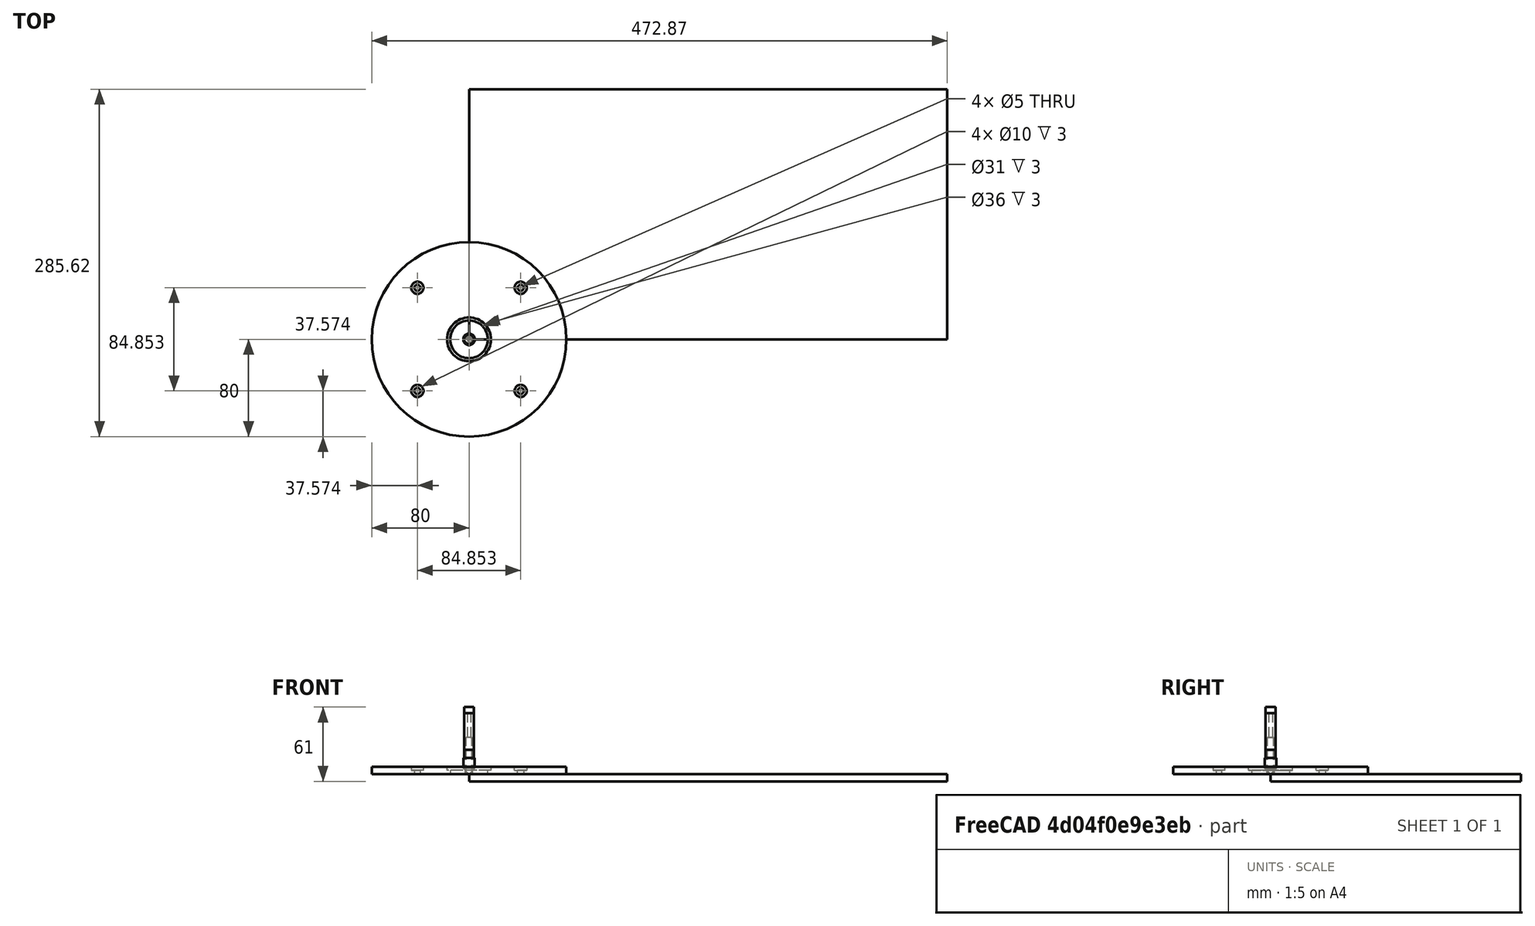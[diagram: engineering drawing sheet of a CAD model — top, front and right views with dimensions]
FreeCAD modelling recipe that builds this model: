
FCSTD DOCUMENT  (FreeCAD 0.22R36874 (Git))
Label: bushing_guide_plate
License: All rights reserved
LicenseURL: http://en.wikipedia.org/wiki/All_rights_reserved
objects: TechDraw::DrawViewDimension×19, Sketcher::SketchObject×13, PartDesign::Pocket×11, Path::FeaturePython×11, PartDesign::PolarPattern×5, Part::FeaturePython×5, App::DocumentObjectGroup×3, PartDesign::Pad×2, PartDesign::Body×2, Spreadsheet::Sheet×1, TechDraw::DrawSVGTemplate×1, App::FeaturePython×1, TechDraw::DrawViewAnnotation×1, PartDesign::Mirrored×1, TechDraw::DrawProjGroupItem×1, TechDraw::DrawProjGroup×1, TechDraw::DrawViewSection×1, TechDraw::DrawPage×1
note: 88 computed .brp shape members not serialized (recipe doc carries the construction recipe); baked Part::Feature solids carry a one-line shape summary decoded from their .brp

FEATURE [Spreadsheet::Sheet] Spreadsheet
  cells = A1='ID; B1(ID)==69 mm; D1='bushing_bore; E1(bushing_bore)==30 mm + 1 mm; A2='OD; B2(OD)==160 mm; D2='bushing_counterbore; E2(bushing_counterbore)==E1 + 5 mm; A3='mounting diameter; B3(mounting_holes_dia)==120 mm; A4='mounting hole; B4(mounting_hole)==5 mm; A7='RT0700_mounting_hole_distance_x; B7(RT0700_mounting_hole_distance_x)==106 mm; A8='RT0700_mounting_hole_distance_y; B8(RT0700_mounting_hole_distance_y)==56 mm
FEATURE [Sketcher::SketchObject] Sketch
  AttachmentSupport = -> [XY_Plane]
  FullyConstrained = true
  MapMode = 5
  expr: Constraints[0] = Spreadsheet.OD + 20 mm
  expr: Constraints[1] = Spreadsheet.ID
  expr: Constraints[5] = 6
  expr: Constraints[7] = Spreadsheet.bushing_bore
  sketch-geometry (6):
    g0: ArcOfCircle CenterX=0 CenterY=0 CenterZ=0 NormalX=0 NormalY=0 NormalZ=1 AngleXU=0 Radius=90 StartAngle=1.34693 EndAngle=4.93625
    g1: ArcOfCircle CenterX=250 CenterY=0 CenterZ=0 NormalX=0 NormalY=0 NormalZ=1 AngleXU=0 Radius=34.5 StartAngle=4.93625 EndAngle=7.63012
    g2: LineSegment StartX=19.98 StartY=87.7542 StartZ=0 EndX=257.659 EndY=33.6391 EndZ=0
    g3: LineSegment StartX=19.98 StartY=-87.7542 StartZ=0 EndX=257.659 EndY=-33.6391 EndZ=0
    g4: Circle CenterX=250 CenterY=0 CenterZ=0 NormalX=0 NormalY=0 NormalZ=1 AngleXU=0 Radius=3
    g5: Circle CenterX=0 CenterY=0 CenterZ=0 NormalX=0 NormalY=0 NormalZ=1 AngleXU=0 Radius=15.5
  constraints (13):
    c: Diameter(g0) = 180
    c: Diameter(g1) = 69
    c: Tangent(g0,g3) = -1.5708
    c: Tangent(g1,g2) = 1.5708
    c: Coincident(g4,g1)
    c: Diameter(g4) = 6
    c: Coincident(g5,g0)
    c: Diameter(g5) = 31
    c: DistanceX(g0,g1) = 250
    c: Tangent(g0,g2) = 1.5708
    c: Tangent(g1,g3) = -1.5708
    c: Coincident(g0,g-1)
    c: PointOnObject(g1,g-1)
FEATURE [PartDesign::Pad] Pad
  Direction = (0,0,1)
  Length = 6
  Length2 = 10
  Profile = -> Sketch
  ReferenceAxis = -> Sketch [N_Axis]
  Suppressed = false
  Type = 0
FEATURE [Sketcher::SketchObject] Sketch001
  AttachmentSupport = -> [Pad]
  FullyConstrained = false
  MapMode = 5
  Placement = pos=(0,0,6) rot=(0,0,1;0rad)
  expr: Constraints[1] = Spreadsheet.mounting_holes_dia
  expr: Constraints[6] = Spreadsheet.mounting_hole
  sketch-geometry (4):
    g0: Circle CenterX=0 CenterY=0 CenterZ=0 NormalX=0 NormalY=0 NormalZ=1 AngleXU=0 Radius=60
    g1: LineSegment StartX=0 StartY=0 StartZ=0 EndX=60 EndY=60 EndZ=0
    g2: GeomPoint X=42.4248 Y=42.428 Z=0
    g3: Circle CenterX=42.4248 CenterY=42.428 CenterZ=0 NormalX=0 NormalY=0 NormalZ=1 AngleXU=0 Radius=2.5
  constraints (7):
    c: Coincident(g0,g-1)
    c: Diameter(g0) = 120
    c: Coincident(g1,g0)
    c: Angle(g-1,g1) = 0.785398
    c: PointOnObject(g2,g0)
    c: Coincident(g3,g2)
    c: Diameter(g3) = 5
FEATURE [PartDesign::Pocket] Pocket
  BaseFeature = -> Pad
  Direction = (0,0,-1)
  Length = 10
  Length2 = 5
  Profile = -> Sketch001
  ReferenceAxis = -> Sketch001 [N_Axis]
  Suppressed = false
  Type = 0
FEATURE [PartDesign::PolarPattern] PolarPattern
  Angle = 360
  Axis = -> Sketch001 [N_Axis]
  BaseFeature = -> Pocket
  Mode = 0
  Occurrences = 4
  Offset = 120
  Originals = -> [Pocket]
  Suppressed = false
FEATURE [TechDraw::DrawSVGTemplate] Template
  EditableTexts = Designed_by_Name=Grzegorz Sapijaszko; Drawing_number=Drawing number; FC-Date=5/24/24; FC-SC=1 : 2; FC-SH=1 / 1; FC-Title=Bushing guide plate; Subtitle=Subtitle; Weight=Weight
  Height = 210
  Orientation = 1
  Template = <userpath>/projekty/woodworking_orig/A4_Landscape_TD.svg
  Width = 297
FEATURE [Sketcher::SketchObject] Sketch002
  AttachmentSupport = -> [PolarPattern]
  ExternalGeometry = -> [PolarPattern]
  FullyConstrained = true
  MapMode = 5
  Placement = pos=(0,0,6) rot=(0,0,1;0rad)
  expr: Constraints[1] = Spreadsheet.mounting_hole * 2
  sketch-geometry (1):
    g0: Circle CenterX=-42.428 CenterY=42.4248 CenterZ=0 NormalX=0 NormalY=0 NormalZ=1 AngleXU=0 Radius=5
  constraints (2):
    c: Coincident(g-3,g0)
    c: Diameter(g0) = 10
FEATURE [PartDesign::Pocket] Pocket001
  BaseFeature = -> PolarPattern
  Direction = (0,0,-1)
  Length = 3
  Length2 = 5
  Profile = -> Sketch002
  ReferenceAxis = -> Sketch002 [N_Axis]
  Suppressed = false
  Type = 0
FEATURE [PartDesign::PolarPattern] PolarPattern001
  Angle = 360
  Axis = -> Sketch002 [N_Axis]
  BaseFeature = -> Pocket001
  Mode = 0
  Occurrences = 4
  Offset = 120
  Originals = -> [Pocket001]
  Suppressed = false
FEATURE [Sketcher::SketchObject] Sketch003
  AttachmentSupport = -> [PolarPattern001]
  ExternalGeometry = -> [PolarPattern001]
  FullyConstrained = true
  MapMode = 5
  Placement = pos=(0,0,6) rot=(0,0,1;0rad)
  expr: Constraints[0] = 12 mm
  sketch-geometry (1):
    g0: Circle CenterX=250 CenterY=0 CenterZ=0 NormalX=0 NormalY=0 NormalZ=1 AngleXU=0 Radius=6
  constraints (2):
    c: Diameter(g0) = 12
    c: Coincident(g-3,g0)
FEATURE [PartDesign::Pocket] Pocket002
  BaseFeature = -> PolarPattern001
  Direction = (0,0,-1)
  Length = 3
  Length2 = 5
  Profile = -> Sketch003
  ReferenceAxis = -> Sketch003 [N_Axis]
  Suppressed = false
  Type = 0
FEATURE [Sketcher::SketchObject] Sketch004
  AttachmentSupport = -> [Pocket002]
  FullyConstrained = true
  MapMode = 5
  Placement = pos=(0,0,6) rot=(0,0,1;0rad)
  expr: Constraints[1] = Spreadsheet.bushing_counterbore
  sketch-geometry (1):
    g0: Circle CenterX=0 CenterY=0 CenterZ=0 NormalX=0 NormalY=0 NormalZ=1 AngleXU=0 Radius=18
  constraints (2):
    c: Coincident(g0,g-1)
    c: Diameter(g0) = 36
FEATURE [PartDesign::Pocket] Pocket003
  BaseFeature = -> Pocket002
  Direction = (0,0,-1)
  Length = 3
  Length2 = 5
  Profile = -> Sketch004
  ReferenceAxis = -> Sketch004 [N_Axis]
  Suppressed = false
  Type = 0
FEATURE [Sketcher::SketchObject] Sketch006
  AttachmentSupport = -> [XY_Plane002]
  FullyConstrained = true
  MapMode = 5
  expr: Constraints[1] = Spreadsheet.OD
  expr: Constraints[3] = Spreadsheet.bushing_bore
  sketch-geometry (2):
    g0: Circle CenterX=0 CenterY=0 CenterZ=0 NormalX=0 NormalY=0 NormalZ=1 AngleXU=0 Radius=80
    g1: Circle CenterX=0 CenterY=0 CenterZ=0 NormalX=0 NormalY=0 NormalZ=1 AngleXU=0 Radius=15.5
  constraints (4):
    c: Coincident(g0,g-1)
    c: Diameter(g0) = 160
    c: Coincident(g1,g0)
    c: Diameter(g1) = 31
FEATURE [PartDesign::Pad] Pad002
  Direction = (0,0,1)
  Length = 6
  Length2 = 10
  Profile = -> Sketch006
  ReferenceAxis = -> Sketch006 [N_Axis]
  Suppressed = false
  Type = 0
FEATURE [Sketcher::SketchObject] Sketch007
  AttachmentSupport = -> [Pad002]
  FullyConstrained = true
  MapMode = 5
  Placement = pos=(0,0,6) rot=(0,0,1;0rad)
  expr: Constraints[1] = Spreadsheet.mounting_holes_dia
  expr: Constraints[6] = Spreadsheet.mounting_hole
  sketch-geometry (3):
    g0: Circle CenterX=0 CenterY=0 CenterZ=0 NormalX=0 NormalY=0 NormalZ=1 AngleXU=0 Radius=60
    g1: LineSegment StartX=0 StartY=0 StartZ=0 EndX=42.4264 EndY=42.4264 EndZ=0
    g2: Circle CenterX=42.4264 CenterY=42.4264 CenterZ=0 NormalX=0 NormalY=0 NormalZ=1 AngleXU=0 Radius=2.5
  constraints (7):
    c: Coincident(g0,g-1)
    c: Diameter(g0) = 120
    c: Coincident(g1,g0)
    c: PointOnObject(g1,g0)
    c: Angle(g-1,g1) = 0.785398
    c: Coincident(g2,g1)
    c: Diameter(g2) = 5
FEATURE [PartDesign::Pocket] Pocket004
  BaseFeature = -> Pad002
  Direction = (0,0,-1)
  Length = 6
  Length2 = 5
  Profile = -> Sketch007
  ReferenceAxis = -> Sketch007 [N_Axis]
  Suppressed = false
  Type = 0
FEATURE [PartDesign::PolarPattern] PolarPattern002
  Angle = 360
  Axis = -> Sketch007 [N_Axis]
  BaseFeature = -> Pocket004
  Mode = 0
  Occurrences = 4
  Offset = 120
  Originals = -> [Pocket004]
  Suppressed = false
FEATURE [Sketcher::SketchObject] Sketch008
  AttachmentSupport = -> [PolarPattern002]
  ExternalGeometry = -> [PolarPattern002]
  FullyConstrained = true
  MapMode = 5
  Placement = pos=(0,0,6) rot=(0,0,1;0rad)
  expr: Constraints[1] = Spreadsheet.mounting_hole * 2
  sketch-geometry (1):
    g0: Circle CenterX=42.4264 CenterY=42.4264 CenterZ=0 NormalX=0 NormalY=0 NormalZ=1 AngleXU=0 Radius=5
  constraints (2):
    c: Coincident(g0,g-3)
    c: Diameter(g0) = 10
FEATURE [PartDesign::Pocket] Pocket005
  BaseFeature = -> PolarPattern002
  Direction = (0,0,-1)
  Length = 3
  Length2 = 5
  Profile = -> Sketch008
  ReferenceAxis = -> Sketch008 [N_Axis]
  Suppressed = false
  Type = 0
FEATURE [PartDesign::PolarPattern] PolarPattern003
  Angle = 360
  Axis = -> Sketch008 [N_Axis]
  BaseFeature = -> Pocket005
  Mode = 0
  Occurrences = 4
  Offset = 120
  Originals = -> [Pocket005]
  Suppressed = false
FEATURE [Sketcher::SketchObject] Sketch009
  AttachmentSupport = -> [PolarPattern003]
  FullyConstrained = true
  MapMode = 5
  Placement = pos=(0,0,6) rot=(0,0,1;0rad)
  expr: Constraints[1] = Spreadsheet.bushing_counterbore
  sketch-geometry (1):
    g0: Circle CenterX=0 CenterY=0 CenterZ=0 NormalX=0 NormalY=0 NormalZ=1 AngleXU=0 Radius=18
  constraints (2):
    c: Coincident(g0,g-1)
    c: Diameter(g0) = 36
FEATURE [PartDesign::Pocket] Pocket006
  BaseFeature = -> PolarPattern003
  Direction = (0,0,-1)
  Length = 3
  Length2 = 5
  Profile = -> Sketch009
  ReferenceAxis = -> Sketch009 [N_Axis]
  Suppressed = false
  Type = 0
FEATURE [PartDesign::Body] Body002  label="bushing_base_plate"
  Group = -> [Sketch006,Pad002,Sketch007,Pocket004,PolarPattern002,Sketch008,Pocket005,PolarPattern003,Sketch009,Pocket006]
  Origin = -> Origin002
  Tip = -> Pocket006
FEATURE [App::FeaturePython] SetupSheet  # Path/CAM operation (typed FeaturePython)
  ClearanceHeightExpression = OpStockZMax+SetupSheet.ClearanceHeightOffset
  ClearanceHeightOffset = 5
  CoolantMode = 0
  CoolantModes = None | Flood | Mist
  FinalDepthExpression = OpFinalDepth
  HorizRapid = 20
  SafeHeightExpression = OpStockZMax+SetupSheet.SafeHeightOffset
  SafeHeightOffset = 3
  StartDepthExpression = OpStartDepth
  StepDownExpression = OpToolDiameter
  VertRapid = 2
FEATURE [Part::FeaturePython] ToolBit  label="Endmill D=6, H=20, S=8"  # Path/CAM toolbit (typed FeaturePython)
  BitPropertyNames = Chipload | CuttingEdgeHeight | Diameter | Flutes | Length | Material | ShankDiameter | SpindleDirection
  BitShape = <path>
  Chipload = 0
  CuttingEdgeHeight = 20
  Diameter = 6
  Flutes = 2
  Length = 50
  Material = 0
  ShankDiameter = 8
  ShapeName = endmill
  SpindleDirection = 0
FEATURE [Path::FeaturePython] TC__Endmill_D_6__H_20__S_8  label="TC: Endmill D=6, H=20, S=8"  # Path/CAM operation (typed FeaturePython)
  HorizFeed = 20
  HorizRapid = 20
  SpindleDir = 0
  SpindleSpeed = 0
  Tool = -> ToolBit
  ToolNumber = 16
  VertFeed = 1.5
  VertRapid = 2
  expr: HorizRapid = SetupSheet.HorizRapid
  expr: VertRapid = SetupSheet.VertRapid
FEATURE [Part::FeaturePython] ToolBit001  label="5mm Endmill"  # Path/CAM toolbit (typed FeaturePython)
  BitPropertyNames = Chipload | CuttingEdgeHeight | Diameter | Flutes | Length | Material | ShankDiameter | SpindleDirection
  BitShape = <userpath>/.local/share/FreeCAD/Macro/Tools/Shape/endmill.fcstd
  Chipload = 0
  CuttingEdgeHeight = 30
  Diameter = 5
  File = <userpath>/.local/share/FreeCAD/Macro/Tools/Bit/5mm_Endmill.fctb
  Flutes = 0
  Length = 50
  Material = 0
  ShankDiameter = 3
  ShapeName = endmill
  SpindleDirection = 0
FEATURE [Path::FeaturePython] TC__5mm_Endmill  label="TC: 5mm Endmill"  # Path/CAM operation (typed FeaturePython)
  HorizFeed = 15
  HorizRapid = 20
  SpindleDir = 0
  SpindleSpeed = 0
  Tool = -> ToolBit001
  ToolNumber = 1
  VertFeed = 2
  VertRapid = 2
  expr: HorizRapid = SetupSheet.HorizRapid
  expr: VertRapid = SetupSheet.VertRapid
FEATURE [Part::FeaturePython] ToolBit002  label="V-bit D=9.5, H=12.7, S=8"  # Path/CAM toolbit (typed FeaturePython)
  BitPropertyNames = Chipload | CuttingEdgeAngle | CuttingEdgeHeight | Diameter | Flutes | Length | Material | ShankDiameter | TipDiameter
  BitShape = <userpath>/.local/share/FreeCAD/Macro/Tools/Shape/vbit.fcstd
  Chipload = 0
  CuttingEdgeAngle = 90
  CuttingEdgeHeight = 8.5
  Diameter = 9.5
  File = <userpath>/.local/share/FreeCAD/Macro/Tools/Bit/1389a496-7324-11ee-af98-1065300da2fe.fctb
  Flutes = 2
  Length = 55
  Material = 0
  ShankDiameter = 8
  ShapeName = vbit
  TipDiameter = 0.1
FEATURE [Path::FeaturePython] TC__V_bit_D_9_5__H_12_7__S_8  label="TC: V-bit D=9.5, H=12.7, S=8"  # Path/CAM operation (typed FeaturePython)
  HorizFeed = 15
  HorizRapid = 20
  SpindleDir = 0
  SpindleSpeed = 0
  Tool = -> ToolBit002
  ToolNumber = 15
  VertFeed = 1
  VertRapid = 2
  expr: HorizRapid = SetupSheet.HorizRapid
  expr: VertRapid = SetupSheet.VertRapid
FEATURE [App::DocumentObjectGroup] Tools
  Group = -> [TC__Endmill_D_6__H_20__S_8,TC__5mm_Endmill,TC__V_bit_D_9_5__H_12_7__S_8]
FEATURE [Sketcher::SketchObject] Sketch010
  AttachmentSupport = -> [Pocket003]
  FullyConstrained = true
  MapMode = 5
  Placement = pos=(0,0,6) rot=(0,0,1;0rad)
  expr: Constraints[0] = Spreadsheet.RT0700_mounting_hole_distance_x / 2
  expr: Constraints[1] = Spreadsheet.RT0700_mounting_hole_distance_y / 2
  expr: Constraints[2] = Spreadsheet.mounting_hole
  expr: Constraints[3] = Spreadsheet.RT0700_mounting_hole_distance_x / 2
  expr: Constraints[4] = Spreadsheet.RT0700_mounting_hole_distance_y / 2
  expr: Constraints[5] = Spreadsheet.mounting_hole
  sketch-geometry (2):
    g0: Circle CenterX=53 CenterY=28 CenterZ=0 NormalX=0 NormalY=0 NormalZ=1 AngleXU=0 Radius=2.5
    g1: Circle CenterX=53 CenterY=-28 CenterZ=0 NormalX=0 NormalY=0 NormalZ=1 AngleXU=0 Radius=2.5
  constraints (6):
    c: DistanceX(g-1,g0) = 53
    c: DistanceY(g-1,g0) = 28
    c: Diameter(g0) = 5
    c: DistanceX(g-1,g1) = 53
    c: DistanceY(g1,g-1) = 28
    c: Diameter(g1) = 5
FEATURE [PartDesign::Pocket] Pocket007
  BaseFeature = -> Pocket003
  Direction = (0,0,-1)
  Length = 6
  Length2 = 5
  Profile = -> Sketch010
  ReferenceAxis = -> Sketch010 [N_Axis]
  Suppressed = false
  Type = 0
FEATURE [Sketcher::SketchObject] Sketch011
  AttachmentSupport = -> [Pocket007]
  ExternalGeometry = -> [Pocket007]
  FullyConstrained = true
  MapMode = 5
  Placement = pos=(0,0,6) rot=(0,0,1;0rad)
  expr: Constraints[1] = Spreadsheet.RT0700_mounting_hole_distance_x / 2
  expr: Constraints[2] = Spreadsheet.RT0700_mounting_hole_distance_y / 2
  expr: Constraints[4] = Spreadsheet.RT0700_mounting_hole_distance_x / 2
  expr: Constraints[5] = Spreadsheet.RT0700_mounting_hole_distance_y / 2
  sketch-geometry (2):
    g0: Circle CenterX=53 CenterY=28 CenterZ=0 NormalX=0 NormalY=0 NormalZ=1 AngleXU=0 Radius=5
    g1: Circle CenterX=53 CenterY=-28 CenterZ=0 NormalX=0 NormalY=0 NormalZ=1 AngleXU=0 Radius=5
  constraints (6):
    c: Diameter(g0) = 10
    c: DistanceX(g-1,g0) = 53
    c: DistanceY(g-1,g0) = 28
    c: Diameter(g1) = 10
    c: DistanceX(g-1,g1) = 53
    c: DistanceY(g1,g-1) = 28
FEATURE [PartDesign::Pocket] Pocket008
  BaseFeature = -> Pocket007
  Direction = (0,0,-1)
  Length = 3
  Length2 = 5
  Profile = -> Sketch011
  ReferenceAxis = -> Sketch011 [N_Axis]
  Suppressed = false
  Type = 0
FEATURE [PartDesign::PolarPattern] PolarPattern004
  Angle = 360
  Axis = -> Sketch010 [N_Axis]
  BaseFeature = -> Pocket008
  Mode = 0
  Occurrences = 4
  Offset = 120
  Originals = -> [Pocket007,Pocket008]
  Suppressed = false
FEATURE [TechDraw::DrawViewAnnotation] Annotation
  Font = osifont
  LineSpace = 100
  LockPosition = false
  MaxWidth = -1
  Rotation = 0
  ScaleType = 0
  Text = 2024-05-23: added mounting holes |        for plunge and trimer bases  |        for Makita RT0700
  TextSize = 4
  TextStyle = 0
  X = 65.4035
  Y = 31.8309
FEATURE [Sketcher::SketchObject] Sketch012
  AttachmentSupport = -> [PolarPattern004]
  FullyConstrained = true
  MapMode = 5
  Placement = pos=(0,0,6) rot=(0,0,1;0rad)
  expr: Constraints[4] = Spreadsheet.mounting_hole
  expr: Constraints[5] = 27.5 mm
  expr: Constraints[7] = Spreadsheet.mounting_hole
  sketch-geometry (3):
    g0: Circle CenterX=0 CenterY=0 CenterZ=0 NormalX=0 NormalY=0 NormalZ=1 AngleXU=0 Radius=35.5
    g1: Circle CenterX=28 CenterY=-25 CenterZ=0 NormalX=0 NormalY=0 NormalZ=1 AngleXU=0 Radius=2.5
    g2: Circle CenterX=27.5 CenterY=20 CenterZ=0 NormalX=0 NormalY=0 NormalZ=1 AngleXU=0 Radius=2.5
  constraints (8):
    c: Coincident(g0,g-1)
    c: Diameter(g0) = 71
    c: DistanceY(g1,g0) = 25
    c: DistanceX(g0,g1) = 28
    c: Diameter(g1) = 5
    c: DistanceX(g0,g2) = 27.5
    c: DistanceY(g0,g2) = 20
    c: Diameter(g2) = 5
FEATURE [PartDesign::Pocket] Pocket009
  BaseFeature = -> PolarPattern004
  Direction = (0,0,-1)
  Length = 6
  Length2 = 5
  Profile = -> Sketch012
  ReferenceAxis = -> Sketch012 [N_Axis]
  Suppressed = false
  Type = 0
FEATURE [Sketcher::SketchObject] Sketch013
  AttachmentSupport = -> [Pocket009]
  ExternalGeometry = -> [Pocket009]
  FullyConstrained = true
  MapMode = 5
  Placement = pos=(0,0,6) rot=(0,0,1;0rad)
  sketch-geometry (2):
    g0: Circle CenterX=27.5 CenterY=20 CenterZ=0 NormalX=0 NormalY=0 NormalZ=1 AngleXU=0 Radius=5
    g1: Circle CenterX=28 CenterY=-25 CenterZ=0 NormalX=0 NormalY=0 NormalZ=1 AngleXU=0 Radius=5
  constraints (4):
    c: Coincident(g0,g-3)
    c: Coincident(g1,g-4)
    c: Diameter(g1) = 10
    c: Diameter(g0) = 10
FEATURE [PartDesign::Pocket] Pocket010
  BaseFeature = -> Pocket009
  Direction = (0,0,-1)
  Length = 3
  Length2 = 5
  Profile = -> Sketch013
  ReferenceAxis = -> Sketch013 [N_Axis]
  Suppressed = false
  Type = 0
FEATURE [PartDesign::Mirrored] Mirrored
  BaseFeature = -> Pocket010
  MirrorPlane = -> Sketch013 [V_Axis]
  Originals = -> [Pocket010,Pocket009]
  Suppressed = false
FEATURE [PartDesign::Body] Body  label="bushing_guide_plate"
  Group = -> [Sketch,Pad,Sketch001,Pocket,PolarPattern,Sketch002,Pocket001,PolarPattern001,Sketch003,Pocket002,Sketch004,Pocket003,Sketch010,Pocket007,Sketch011,Pocket008,PolarPattern004,Sketch012,Pocket009,Sketch013,Pocket010,Mirrored]
  Origin = -> Origin
  Tip = -> Mirrored
FEATURE [TechDraw::DrawProjGroupItem] ProjItem  label="Front"
  CoarseView = false
  Direction = (0,0,1)
  Focus = 100
  HardHidden = false
  IsoCount = 0
  IsoHidden = false
  IsoVisible = false
  LockPosition = true
  Perspective = false
  Rotation = 0
  RotationVector = (1,0,0)
  Scale = 0.5
  ScaleType = 2
  ScrubCount = 0
  SeamHidden = false
  SeamVisible = false
  SmoothHidden = false
  SmoothVisible = true
  Source = -> [Body]
  Type = 0
  X = 0
  XDirection = (1,0,0)
  Y = 0
FEATURE [TechDraw::DrawProjGroup] ProjGroup
  Anchor = -> ProjItem
  AutoDistribute = true
  LockPosition = false
  ProjectionType = 0
  Rotation = 0
  Scale = 0.5
  ScaleType = 2
  Source = -> [Body]
  Views = -> [ProjItem]
  X = 150
  Y = 145
  spacingX = 15
  spacingY = 15
FEATURE [TechDraw::DrawViewSection] SectionView  label="Section  - "
  BaseView = -> ProjItem
  CoarseView = false
  CutSurfaceDisplay = 2
  Direction = (1e-16,-1,0)
  FileGeomPattern = <path>
  FileHatchPattern = <path>
  Focus = 100
  FuseBeforeCut = false
  HardHidden = false
  HatchOffset = (0,0,0)
  HatchRotation = 0
  HatchScale = 1
  IsoCount = 0
  IsoHidden = false
  IsoVisible = false
  LockPosition = false
  NameGeomPattern = Diamond
  Perspective = false
  Rotation = 0
  Scale = 0.5
  ScaleType = 2
  ScrubCount = 0
  SeamHidden = false
  SeamVisible = false
  SectionDirection = 4
  SectionLineStretch = 1
  SectionNormal = (1e-16,-1,0)
  SectionOrigin = (97.29,-0.05,5)
  SmoothHidden = false
  SmoothVisible = true
  Source = -> [Body]
  TrimAfterCut = false
  UsePreviousCut = false
  X = 150
  XDirection = (1,1e-16,0)
  Y = 70
FEATURE [TechDraw::DrawViewDimension] Dimension
  AngleOverride = false
  Arbitrary = false
  ArbitraryTolerances = false
  BoxCorners = (2) [(-93.625,-1.5,-1e-07),(93.625,1.5,1e-07)]
  EqualTolerance = true
  ExtensionAngle = 0
  FormatSpec = ⌀%.2w
  FormatSpecOverTolerance = %+.2w
  FormatSpecUnderTolerance = %+.2w
  Inverted = false
  LineAngle = 0
  LockPosition = false
  MeasureType = 1
  OverTolerance = 0
  References2D = -> [SectionView]
  Rotation = 0
  ScaleType = 0
  TheoreticalExact = false
  Type = 1
  UnderTolerance = 0
  X = -48.625
  Y = -2.70318
FEATURE [TechDraw::DrawViewDimension] Dimension002
  AngleOverride = false
  Arbitrary = false
  ArbitraryTolerances = false
  BoxCorners = (2) [(-93.625,-1.5,-1e-07),(93.625,1.5,1e-07)]
  EqualTolerance = true
  ExtensionAngle = 0
  FormatSpec = ⌀%.2w
  FormatSpecOverTolerance = %+.2w
  FormatSpecUnderTolerance = %+.2w
  Inverted = false
  LineAngle = 0
  LockPosition = false
  MeasureType = 1
  OverTolerance = 0
  References2D = -> [SectionView]
  Rotation = 0
  ScaleType = 0
  TheoreticalExact = false
  Type = 1
  UnderTolerance = 0
  X = -48.625
  Y = 12.5693
FEATURE [TechDraw::DrawViewDimension] Dimension006
  AngleOverride = false
  Arbitrary = false
  ArbitraryTolerances = false
  BoxCorners = (2) [(-93.625,-45,0),(93.625,45,0)]
  EqualTolerance = true
  ExtensionAngle = 0
  FormatSpec = R%.2w
  FormatSpecOverTolerance = %+.2w
  FormatSpecUnderTolerance = %+.2w
  Inverted = false
  LineAngle = 0
  LockPosition = false
  MeasureType = 1
  OverTolerance = 0
  References2D = -> [ProjItem]
  Rotation = 0
  ScaleType = 0
  TheoreticalExact = false
  Type = 4
  UnderTolerance = 0
  X = 99.6814
  Y = 13.0174
FEATURE [TechDraw::DrawViewDimension] Dimension008
  AngleOverride = false
  Arbitrary = false
  ArbitraryTolerances = false
  BoxCorners = (2) [(-93.625,-45,0),(93.625,45,0)]
  EqualTolerance = true
  ExtensionAngle = 0
  FormatSpec = R%.2w
  FormatSpecOverTolerance = %+.2w
  FormatSpecUnderTolerance = %+.2w
  Inverted = false
  LineAngle = 0
  LockPosition = false
  MeasureType = 1
  OverTolerance = 0
  References2D = -> [ProjItem]
  Rotation = 0
  ScaleType = 0
  TheoreticalExact = false
  Type = 4
  UnderTolerance = 0
  X = -54.8187
  Y = 39.2993
FEATURE [TechDraw::DrawViewDimension] Dimension010
  AngleOverride = false
  Arbitrary = false
  ArbitraryTolerances = false
  BoxCorners = (2) [(-93.625,-1.5,-1e-07),(93.625,1.5,1e-07)]
  EqualTolerance = true
  ExtensionAngle = 0
  FormatSpec = %.2w
  FormatSpecOverTolerance = %+.2w
  FormatSpecUnderTolerance = %+.2w
  Inverted = false
  LineAngle = 0
  LockPosition = false
  MeasureType = 1
  OverTolerance = 0
  References2D = -> [SectionView]
  Rotation = 0
  ScaleType = 0
  TheoreticalExact = false
  Type = 2
  UnderTolerance = 0
  X = -100.968
  Y = 2.5
FEATURE [Part::FeaturePython] Clone  label="Model-bushing_guide_plate"  # Draft clone (typed FeaturePython)
  AttacherType = Attacher::AttachEngine3D
  Fuse = false
  Objects = -> [Body]
  PathResource = Model
  Placement = pos=(105,104.973,-6) rot=(0,0,-1;0.226893rad)
  Scale = (1,1,1)
FEATURE [App::DocumentObjectGroup] Model
  Group = -> [Clone]
FEATURE [Part::FeaturePython] Stock  # WARN: FeaturePython — macro-defined, semantics opaque (R4)
  Base = -> Model
  ExtXneg = 15
  ExtXpos = 10
  ExtYneg = 15
  ExtYpos = 10
  ExtZneg = 0
  ExtZpos = 0
  Placement = pos=(15,15,-6) rot=(0,0,1;0rad)
  StockType = FromBase
FEATURE [Path::FeaturePython] Adaptive  # Path/CAM operation (typed FeaturePython)
  Active = true
  Base = -> [Clone]
  ClearanceHeight = 5
  CoolantMode = 0
  CycleTime = 00:18:50
  ExtensionCorners = true
  ExtensionLengthDefault = 3
  FinalDepth = -3
  FinishDepth = 0
  FinishingProfile = true
  ForceInsideOut = false
  HelixAngle = 5
  HelixConeAngle = 0
  HelixDiameterLimit = 1
  KeepToolDownRatio = 3
  LiftDistance = 0
  OpFinalDepth = 0
  OpStartDepth = 1
  OpStockZMax = 0
  OpStockZMin = -6
  OpToolDiameter = 6
  OperationType = 1
  SafeHeight = 3
  Side = 1
  StartDepth = 0
  StepDown = 1
  StepOver = 20
  StockToLeave = 0
  StopProcessing = false
  Stopped = false
  Tolerance = 0.1
  ToolController = -> TC__Endmill_D_6__H_20__S_8
  UseHelixArcs = false
  UseOutline = false
  expr: ClearanceHeight = OpStockZMax + SetupSheet.ClearanceHeightOffset
  expr: ExtensionLengthDefault = OpToolDiameter / 2
  expr: FinalDepth = -3 mm
  expr: SafeHeight = OpStockZMax + SetupSheet.SafeHeightOffset
  expr: StartDepth = 0
  expr: StepDown = 1 mm
FEATURE [Path::FeaturePython] Adaptive001  # Path/CAM operation (typed FeaturePython)
  Active = true
  Base = -> [Clone]
  ClearanceHeight = 5
  CoolantMode = 0
  CycleTime = 00:02:35
  ExtensionCorners = true
  ExtensionLengthDefault = 3
  FinalDepth = -3
  FinishDepth = 0
  FinishingProfile = true
  ForceInsideOut = false
  HelixAngle = 5
  HelixConeAngle = 0
  HelixDiameterLimit = 0
  KeepToolDownRatio = 3
  LiftDistance = 0
  OpFinalDepth = -3
  OpStartDepth = 0
  OpStockZMax = 0
  OpStockZMin = -6
  OpToolDiameter = 6
  OperationType = 0
  SafeHeight = 3
  Side = 1
  StartDepth = 0
  StepDown = 1
  StepOver = 30
  StockToLeave = 0
  StopProcessing = false
  Stopped = false
  Tolerance = 0.1
  ToolController = -> TC__Endmill_D_6__H_20__S_8
  UseHelixArcs = false
  UseOutline = false
  expr: ClearanceHeight = OpStockZMax + SetupSheet.ClearanceHeightOffset
  expr: ExtensionLengthDefault = OpToolDiameter / 2
  expr: FinalDepth = OpFinalDepth
  expr: SafeHeight = OpStockZMax + SetupSheet.SafeHeightOffset
  expr: StartDepth = OpStartDepth
  expr: StepDown = 1
FEATURE [Path::FeaturePython] Adaptive002  # Path/CAM operation (typed FeaturePython)
  Active = true
  Base = -> [Clone]
  ClearanceHeight = 5
  CoolantMode = 0
  CycleTime = 00:03:15
  ExtensionCorners = true
  ExtensionLengthDefault = 3
  FinalDepth = -7
  FinishDepth = 0
  FinishingProfile = true
  ForceInsideOut = false
  HelixAngle = 5
  HelixConeAngle = 0
  HelixDiameterLimit = 0
  KeepToolDownRatio = 3
  LiftDistance = 0
  OpFinalDepth = -6
  OpStartDepth = 0
  OpStockZMax = 0
  OpStockZMin = -6
  OpToolDiameter = 6
  OperationType = 0
  SafeHeight = 3
  Side = 1
  StartDepth = -3
  StepDown = 1
  StepOver = 30
  StockToLeave = 0
  StopProcessing = false
  Stopped = false
  Tolerance = 0.1
  ToolController = -> TC__Endmill_D_6__H_20__S_8
  UseHelixArcs = false
  UseOutline = false
  expr: ClearanceHeight = OpStockZMax + SetupSheet.ClearanceHeightOffset
  expr: ExtensionLengthDefault = OpToolDiameter / 2
  expr: FinalDepth = OpFinalDepth - 1 mm
  expr: SafeHeight = OpStockZMax + SetupSheet.SafeHeightOffset
  expr: StartDepth = -3 mm
  expr: StepDown = 1
FEATURE [Path::FeaturePython] Adaptive003  # Path/CAM operation (typed FeaturePython)
  Active = true
  Base = -> [Clone]
  ClearanceHeight = 5
  CoolantMode = 0
  CycleTime = 01:13:24
  ExtensionCorners = true
  ExtensionLengthDefault = 2.5
  FinalDepth = -7
  FinishDepth = 0
  FinishingProfile = true
  ForceInsideOut = false
  HelixAngle = 5
  HelixConeAngle = 0
  HelixDiameterLimit = 0
  KeepToolDownRatio = 3
  LiftDistance = 0
  OpFinalDepth = -6
  OpStartDepth = 0
  OpStockZMax = 0
  OpStockZMin = -6
  OpToolDiameter = 5
  OperationType = 1
  SafeHeight = 3
  Side = 0
  StartDepth = 0
  StepDown = 1
  StepOver = 40
  StockToLeave = 0.5
  StopProcessing = false
  Stopped = false
  Tolerance = 0.05
  ToolController = -> TC__5mm_Endmill
  UseHelixArcs = false
  UseOutline = false
  expr: ClearanceHeight = OpStockZMax + SetupSheet.ClearanceHeightOffset
  expr: ExtensionLengthDefault = OpToolDiameter / 2
  expr: FinalDepth = OpFinalDepth - 1 mm
  expr: SafeHeight = OpStockZMax + SetupSheet.SafeHeightOffset
  expr: StartDepth = OpStartDepth
  expr: StepDown = 1
FEATURE [Path::FeaturePython] Drilling  # Path/CAM operation (typed FeaturePython)
  Active = true
  AddTipLength = false
  Base = -> [Clone]
  ClearanceHeight = 5
  CoolantMode = 0
  CycleTime = 00:00:33
  DwellEnabled = false
  DwellTime = 1
  ExtraOffset = 0
  FinalDepth = -7
  KeepToolDown = false
  OpFinalDepth = -6
  OpStartDepth = 0
  OpStockZMax = 0
  OpStockZMin = -6
  OpToolDiameter = 5
  PeckDepth = 1
  PeckEnabled = true
  RetractHeight = 0
  RetractMode = 0
  SafeHeight = 3
  StartDepth = -3
  ToolController = -> TC__5mm_Endmill
  chipBreakEnabled = false
  feedRetractEnabled = false
  expr: ClearanceHeight = OpStockZMax + SetupSheet.ClearanceHeightOffset
  expr: FinalDepth = OpFinalDepth - 1 mm
  expr: PeckDepth = 1 mm
  expr: RetractHeight = StartDepth + SetupSheet.SafeHeightOffset
  expr: SafeHeight = OpStockZMax + SetupSheet.SafeHeightOffset
  expr: StartDepth = -3
FEATURE [Path::FeaturePython] Deburr  # Path/CAM operation (typed FeaturePython)
  Active = true
  Base = -> [Clone]
  ClearanceHeight = 5
  CoolantMode = 0
  CycleTime = 00:01:16
  Direction = 0
  EntryPoint = 0
  ExtraDepth = 0.5
  Join = 0
  OpStockZMax = 0
  OpStockZMin = -6
  OpToolDiameter = 9.5
  SafeHeight = 3
  Side = 0
  StartDepth = 0
  StepDown = 0
  ToolController = -> TC__V_bit_D_9_5__H_12_7__S_8
  Width = 0.8
  expr: ClearanceHeight = OpStockZMax + SetupSheet.ClearanceHeightOffset
  expr: SafeHeight = OpStockZMax + SetupSheet.SafeHeightOffset
  expr: StepDown = 0 mm
FEATURE [TechDraw::DrawViewDimension] Dimension014
  AngleOverride = false
  Arbitrary = false
  ArbitraryTolerances = false
  BoxCorners = (2) [(-93.625,-45,0),(93.625,45,0)]
  EqualTolerance = true
  ExtensionAngle = 0
  FormatSpec = %.2w
  FormatSpecOverTolerance = %+.2w
  FormatSpecUnderTolerance = %+.2w
  Inverted = false
  LineAngle = 0
  LockPosition = false
  MeasureType = 1
  OverTolerance = 0
  References2D = -> [ProjItem]
  Rotation = 0
  ScaleType = 0
  TheoreticalExact = false
  Type = 1
  UnderTolerance = 0
  X = -48.7181
  Y = -45.8833
FEATURE [TechDraw::DrawViewDimension] Dimension015
  AngleOverride = false
  Arbitrary = false
  ArbitraryTolerances = false
  BoxCorners = (2) [(-93.625,-45,0),(93.625,45,0)]
  EqualTolerance = true
  ExtensionAngle = 0
  FormatSpec = %.2w
  FormatSpecOverTolerance = %+.2w
  FormatSpecUnderTolerance = %+.2w
  Inverted = false
  LineAngle = 0
  LockPosition = false
  MeasureType = 1
  OverTolerance = 0
  References2D = -> [ProjItem]
  Rotation = 0
  ScaleType = 0
  TheoreticalExact = false
  Type = 1
  UnderTolerance = 0
  X = -47.9755
  Y = -32.2815
FEATURE [TechDraw::DrawViewDimension] Dimension016
  AngleOverride = false
  Arbitrary = false
  ArbitraryTolerances = false
  BoxCorners = (2) [(-93.625,-45,0),(93.625,45,0)]
  EqualTolerance = true
  ExtensionAngle = 0
  FormatSpec = %.2w
  FormatSpecOverTolerance = %+.2w
  FormatSpecUnderTolerance = %+.2w
  Inverted = false
  LineAngle = 0
  LockPosition = false
  MeasureType = 1
  OverTolerance = 0
  References2D = -> [ProjItem]
  Rotation = 0
  ScaleType = 0
  TheoreticalExact = false
  Type = 2
  UnderTolerance = 0
  X = -112.246
  Y = 6.71762
FEATURE [TechDraw::DrawViewDimension] Dimension017
  AngleOverride = false
  Arbitrary = false
  ArbitraryTolerances = false
  BoxCorners = (2) [(-93.625,-45,0),(93.625,45,0)]
  EqualTolerance = true
  ExtensionAngle = 0
  FormatSpec = %.2w
  FormatSpecOverTolerance = %+.2w
  FormatSpecUnderTolerance = %+.2w
  Inverted = false
  LineAngle = 0
  LockPosition = false
  MeasureType = 1
  OverTolerance = 0
  References2D = -> [ProjItem]
  Rotation = 0
  ScaleType = 0
  TheoreticalExact = false
  Type = 7
  UnderTolerance = 0
  X = -4.10908
  Y = 21.0252
FEATURE [TechDraw::DrawViewDimension] Dimension018
  AngleOverride = false
  Arbitrary = false
  ArbitraryTolerances = false
  BoxCorners = (2) [(-93.625,-45,0),(93.625,45,0)]
  EqualTolerance = true
  ExtensionAngle = 0
  FormatSpec = %.2w
  FormatSpecOverTolerance = %+.2w
  FormatSpecUnderTolerance = %+.2w
  Inverted = false
  LineAngle = 0
  LockPosition = false
  MeasureType = 1
  OverTolerance = 0
  References2D = -> [ProjItem]
  Rotation = 0
  ScaleType = 0
  TheoreticalExact = false
  Type = 2
  UnderTolerance = 0
  X = -119.337
  Y = 6.22435
FEATURE [TechDraw::DrawViewDimension] Dimension019
  AngleOverride = false
  Arbitrary = false
  ArbitraryTolerances = false
  BoxCorners = (2) [(-93.625,-45,0),(93.625,45,0)]
  EqualTolerance = true
  ExtensionAngle = 0
  FormatSpec = ⌀%.2w
  FormatSpecOverTolerance = %+.2w
  FormatSpecUnderTolerance = %+.2w
  Inverted = false
  LineAngle = 0
  LockPosition = false
  MeasureType = 1
  OverTolerance = 0
  References2D = -> [ProjItem]
  Rotation = 0
  ScaleType = 0
  TheoreticalExact = false
  Type = 5
  UnderTolerance = 0
  X = -12.1681
  Y = -13.3994
FEATURE [TechDraw::DrawViewDimension] Dimension020
  AngleOverride = false
  Arbitrary = false
  ArbitraryTolerances = false
  BoxCorners = (2) [(-93.625,-45,0),(93.625,45,0)]
  EqualTolerance = true
  ExtensionAngle = 0
  FormatSpec = ⌀%.2w
  FormatSpecOverTolerance = %+.2w
  FormatSpecUnderTolerance = %+.2w
  Inverted = false
  LineAngle = 0
  LockPosition = false
  MeasureType = 1
  OverTolerance = 0
  References2D = -> [ProjItem]
  Rotation = 0
  ScaleType = 0
  TheoreticalExact = false
  Type = 5
  UnderTolerance = 0
  X = -13.0372
  Y = -2.67988
FEATURE [TechDraw::DrawViewDimension] Dimension021
  AngleOverride = false
  Arbitrary = false
  ArbitraryTolerances = false
  BoxCorners = (2) [(-93.625,-45,0),(93.625,45,0)]
  EqualTolerance = true
  ExtensionAngle = 0
  FormatSpec = %.2w
  FormatSpecOverTolerance = %+.2w
  FormatSpecUnderTolerance = %+.2w
  Inverted = false
  LineAngle = 0
  LockPosition = false
  MeasureType = 1
  OverTolerance = 0
  References2D = -> [ProjItem]
  Rotation = 0
  ScaleType = 0
  TheoreticalExact = false
  Type = 1
  UnderTolerance = 0
  X = -41.642
  Y = 24.1326
FEATURE [TechDraw::DrawViewDimension] Dimension022
  AngleOverride = false
  Arbitrary = false
  ArbitraryTolerances = false
  BoxCorners = (2) [(-93.625,-45,0),(93.625,45,0)]
  EqualTolerance = true
  ExtensionAngle = 0
  FormatSpec = %.2w
  FormatSpecOverTolerance = %+.2w
  FormatSpecUnderTolerance = %+.2w
  Inverted = false
  LineAngle = 0
  LockPosition = false
  MeasureType = 1
  OverTolerance = 0
  References2D = -> [ProjItem]
  Rotation = 0
  ScaleType = 0
  TheoreticalExact = false
  Type = 2
  UnderTolerance = 0
  X = -32.6776
  Y = 7.5
FEATURE [TechDraw::DrawViewDimension] Dimension023
  AngleOverride = false
  Arbitrary = false
  ArbitraryTolerances = false
  BoxCorners = (2) [(-93.625,-45,0),(93.625,45,0)]
  EqualTolerance = true
  ExtensionAngle = 0
  FormatSpec = %.2w
  FormatSpecOverTolerance = %+.2w
  FormatSpecUnderTolerance = %+.2w
  Inverted = false
  LineAngle = 0
  LockPosition = false
  MeasureType = 1
  OverTolerance = 0
  References2D = -> [ProjItem]
  Rotation = 0
  ScaleType = 0
  TheoreticalExact = false
  Type = 2
  UnderTolerance = 0
  X = -32.6776
  Y = -3.75
FEATURE [TechDraw::DrawViewDimension] Dimension024
  AngleOverride = false
  Arbitrary = false
  ArbitraryTolerances = false
  BoxCorners = (2) [(-93.625,-45,0),(93.625,45,0)]
  EqualTolerance = true
  ExtensionAngle = 0
  FormatSpec = %.2w
  FormatSpecOverTolerance = %+.2w
  FormatSpecUnderTolerance = %+.2w
  Inverted = false
  LineAngle = 0
  LockPosition = false
  MeasureType = 1
  OverTolerance = 0
  References2D = -> [ProjItem]
  Rotation = 0
  ScaleType = 0
  TheoreticalExact = false
  Type = 1
  UnderTolerance = 0
  X = -41.841
  Y = -12.8223
FEATURE [TechDraw::DrawViewDimension] Dimension025
  AngleOverride = false
  Arbitrary = false
  ArbitraryTolerances = false
  BoxCorners = (2) [(-93.625,-1.5,-1e-07),(93.625,1.5,1e-07)]
  EqualTolerance = true
  ExtensionAngle = 0
  FormatSpec = ⌀%.2w
  FormatSpecOverTolerance = %+.2w
  FormatSpecUnderTolerance = %+.2w
  Inverted = false
  LineAngle = 0
  LockPosition = false
  MeasureType = 1
  OverTolerance = 0
  References2D = -> [SectionView]
  Rotation = 0
  ScaleType = 0
  TheoreticalExact = false
  Type = 1
  UnderTolerance = 0
  X = 82.7694
  Y = -1.78018
FEATURE [Path::FeaturePython] Drilling001  # Path/CAM operation (typed FeaturePython)
  Active = true
  AddTipLength = false
  Base = -> [Clone]
  ClearanceHeight = 5
  CoolantMode = 0
  CycleTime = 00:00:25
  DwellEnabled = false
  DwellTime = 1
  ExtraOffset = 0
  FinalDepth = -6
  KeepToolDown = false
  OpFinalDepth = -6
  OpStartDepth = 0
  OpStockZMax = 0
  OpStockZMin = -6
  OpToolDiameter = 6
  PeckDepth = 1
  PeckEnabled = true
  RetractHeight = 0
  RetractMode = 0
  SafeHeight = 3
  StartDepth = -3
  ToolController = -> TC__Endmill_D_6__H_20__S_8
  chipBreakEnabled = false
  feedRetractEnabled = false
  expr: ClearanceHeight = OpStockZMax + SetupSheet.ClearanceHeightOffset
  expr: FinalDepth = OpFinalDepth
  expr: PeckDepth = 1 mm
  expr: RetractHeight = StartDepth + SetupSheet.SafeHeightOffset
  expr: SafeHeight = OpStockZMax + SetupSheet.SafeHeightOffset
  expr: StartDepth = -3 mm
FEATURE [App::DocumentObjectGroup] Operations
  Group = -> [Adaptive,Drilling001,Drilling,Adaptive001,Adaptive002,Adaptive003,Deburr]
FEATURE [Path::FeaturePython] Job  label="Job_bushing_guide_plate"  # Path/CAM operation (typed FeaturePython)
  CycleTime = 01:40:18
  Fixtures = G54
  GeometryTolerance = 0.01
  JobType = 0
  Model = -> Model
  Operations = -> Operations
  OrderOutputBy = 2
  PostProcessor = 3
  PostProcessorOutputFile = %D/%O_%t_%d.gcode
  SetupSheet = -> SetupSheet
  SplitOutput = true
  Stock = -> Stock
  Tools = -> Tools
FEATURE [TechDraw::DrawViewDimension] Dimension026
  AngleOverride = false
  Arbitrary = false
  ArbitraryTolerances = false
  BoxCorners = (2) [(-93.625,-1.5,-1e-07),(93.625,1.5,1e-07)]
  EqualTolerance = true
  ExtensionAngle = 0
  FormatSpec = ⌀%.2w
  FormatSpecOverTolerance = %+.2w
  FormatSpecUnderTolerance = %+.2w
  Inverted = false
  LineAngle = 0
  LockPosition = false
  MeasureType = 1
  OverTolerance = 0
  References2D = -> [SectionView]
  Rotation = 0
  ScaleType = 0
  TheoreticalExact = false
  Type = 1
  UnderTolerance = 0
  X = 76.0168
  Y = 13.8691
FEATURE [TechDraw::DrawViewDimension] Dimension027
  AngleOverride = false
  Arbitrary = false
  ArbitraryTolerances = false
  BoxCorners = (2) [(-93.625,-1.5,-1e-07),(93.625,1.5,1e-07)]
  EqualTolerance = true
  ExtensionAngle = 0
  FormatSpec = %.2w
  FormatSpecOverTolerance = %+.2w
  FormatSpecUnderTolerance = %+.2w
  Inverted = false
  LineAngle = 0
  LockPosition = false
  MeasureType = 1
  OverTolerance = 0
  References2D = -> [SectionView]
  Rotation = 0
  ScaleType = 0
  TheoreticalExact = false
  Type = 2
  UnderTolerance = 0
  X = 95.2132
  Y = 8.42332
FEATURE [TechDraw::DrawPage] Page
  KeepUpdated = true
  NextBalloonIndex = 1
  ProjectionType = 0
  Template = -> Template
  Views = -> [ProjGroup,SectionView,Dimension,Dimension002,Dimension006,Dimension008,Dimension010,Dimension014,Dimension015,Dimension016,Dimension017,Dimension018,Dimension019,Dimension020,Annotation,Dimension021,Dimension022,Dimension023,Dimension024,Dimension025,Dimension026,Dimension027]
note: 3 file-system paths scrubbed to <path> (originals preserved in the JSON sidecar)
